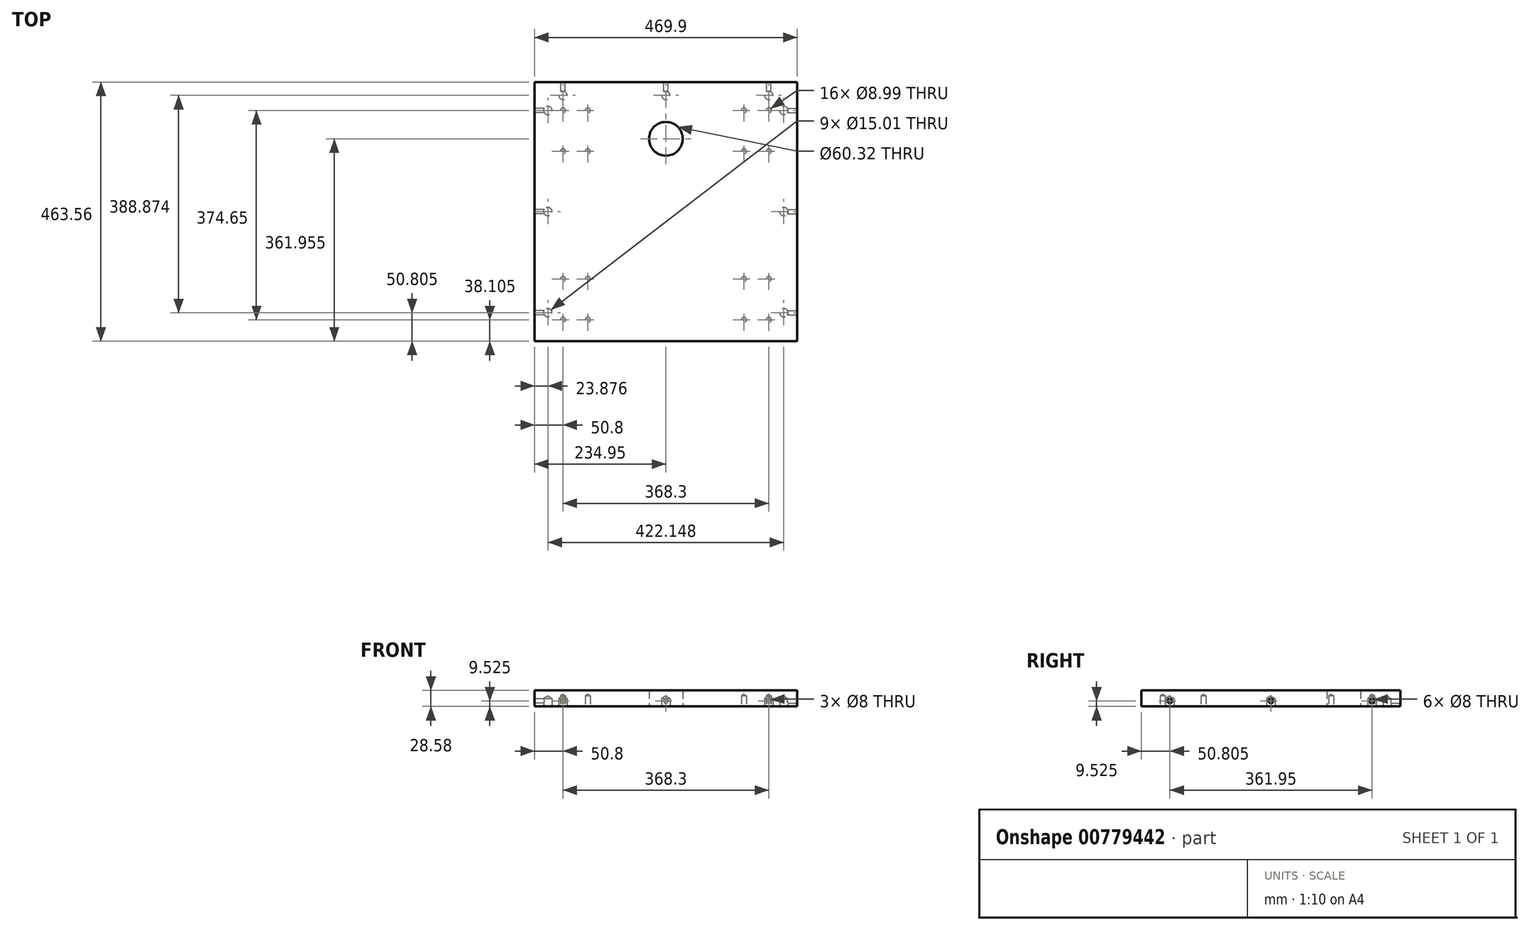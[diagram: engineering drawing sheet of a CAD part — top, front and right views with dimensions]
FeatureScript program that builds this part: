
annotation { "Feature Type Name" : "Feature", "Feature Type Description" : "" }
export const myFeature = defineFeature(function(context is Context, id is Id, definition is map)
    precondition{}
    {
        {
            var Q0;
            Q0=qCreatedBy(makeId("Top.planeOp"),FACE);
            var sketch = newSketch(context, id + "F0", { "sketchPlane" : qUnion([Q0])});
            skLineSegment(sketch, "E0.bottom", {"start": v(234.95, 231.78) * mm, "end": v(-234.95, 231.78) * mm});
            skLineSegment(sketch, "E0.top", {"start": v(234.95, -231.78) * mm, "end": v(-234.95, -231.78) * mm});
            skLineSegment(sketch, "E0.left", {"start": v(234.95, 231.77) * mm, "end": v(234.95, -231.78) * mm});
            skLineSegment(sketch, "E0.right", {"start": v(-234.95, 231.78) * mm, "end": v(-234.95, -231.78) * mm});
            skPoint(sketch, "E0.middle", {"position": v(0, 0) * mm});
            skSolve(sketch);
        }
        {
            var Q0;
            Q0=makeQuery(id+"F0.imprint","IMPRINT",FACE,{"disambiguationData":[TD([[makeQuery(id+"F0.imprint","IMPRINT",EDGE,{"derivedFrom":sQuery(id+"F0.wireOp",EDGE,"E0.bottom")}),1.0]])]});
            extrude(context, id + "F1", {"entities" : qUnion([Q0]), "depth" : 19.05 * mm, "offsetDistance" : 25.4 * mm});
        }
        {
            var Q0;
            Q0=makeQuery(id+"F1.opExtrude","CAP_FACE",FACE,{"disambiguationData":[OSD([sQuery(id+"F0.wireOp",EDGE,"E0.bottom"),sQuery(id+"F0.wireOp",EDGE,"E0.top"),sQuery(id+"F0.wireOp",EDGE,"E0.left"),sQuery(id+"F0.wireOp",EDGE,"E0.right")])],"isStart":true});
            var sketch = newSketch(context, id + "F2", { "sketchPlane" : qUnion([Q0])});
            skLineSegment(sketch, "E1", {"start": v(-234.95, 231.78) * mm, "end": v(-211.07, 231.78) * mm});
            skLineSegment(sketch, "E2", {"start": v(-211.07, 231.78) * mm, "end": v(-211.07, 180.97) * mm});
            skLineSegment(sketch, "E3", {"start": v(-234.95, -231.78) * mm, "end": v(-211.07, -231.78) * mm});
            skLineSegment(sketch, "E4", {"start": v(-211.07, -231.78) * mm, "end": v(-211.07, -180.97) * mm});
            skLineSegment(sketch, "E5", {"start": v(234.95, 231.78) * mm, "end": v(234.95, 207.9) * mm});
            skLineSegment(sketch, "E6", {"start": v(234.95, 231.78) * mm, "end": v(211.07, 231.78) * mm});
            skLineSegment(sketch, "E7", {"start": v(211.07, 231.78) * mm, "end": v(211.07, 180.97) * mm});
            skLineSegment(sketch, "E8", {"start": v(234.95, -231.78) * mm, "end": v(211.07, -231.78) * mm});
            skLineSegment(sketch, "E9", {"start": v(211.07, -231.78) * mm, "end": v(211.07, -180.97) * mm});
            skLineSegment(sketch, "E10", {"start": v(-234.95, 0) * mm, "end": v(-211.07, 0) * mm});
            skLineSegment(sketch, "E11", {"start": v(234.95, 0) * mm, "end": v(211.07, 0) * mm});
            skLineSegment(sketch, "E12", {"start": v(0, -231.78) * mm, "end": v(0, -207.9) * mm});
            skLineSegment(sketch, "E13", {"start": v(-234.95, -231.78) * mm, "end": v(-234.95, -207.9) * mm});
            skLineSegment(sketch, "E14", {"start": v(-234.95, -207.9) * mm, "end": v(-184.15, -207.9) * mm});
            skLineSegment(sketch, "E15", {"start": v(234.95, -231.78) * mm, "end": v(234.95, -207.9) * mm});
            skLineSegment(sketch, "E16", {"start": v(234.95, -207.9) * mm, "end": v(184.15, -207.9) * mm});
            skPoint(sketch, "E17", {"position": v(-211.07, 180.97) * mm});
            skPoint(sketch, "E18", {"position": v(211.07, 180.97) * mm});
            skPoint(sketch, "E19", {"position": v(211.07, 0) * mm});
            skPoint(sketch, "E20", {"position": v(-211.07, 0) * mm});
            skPoint(sketch, "E21", {"position": v(-211.07, -180.97) * mm});
            skPoint(sketch, "E22", {"position": v(-184.15, -207.9) * mm});
            skPoint(sketch, "E23", {"position": v(0, -207.9) * mm});
            skPoint(sketch, "E24", {"position": v(184.15, -207.9) * mm});
            skPoint(sketch, "E25", {"position": v(211.07, -180.97) * mm});
            skSolve(sketch);
        }
        {
            var Q0;
            Q0=sQuery(id+"F2.wireOp",VERTEX,"E17");
            var Q1;
            Q1=sQuery(id+"F2.wireOp",VERTEX,"E20");
            var Q2;
            Q2=sQuery(id+"F2.wireOp",VERTEX,"E21");
            var Q3;
            Q3=sQuery(id+"F2.wireOp",VERTEX,"E22");
            var Q4;
            Q4=sQuery(id+"F2.wireOp",VERTEX,"E23");
            var Q5;
            Q5=sQuery(id+"F2.wireOp",VERTEX,"E24");
            var Q6;
            Q6=sQuery(id+"F2.wireOp",VERTEX,"E25");
            var Q7;
            Q7=sQuery(id+"F2.wireOp",VERTEX,"E19");
            var Q8;
            Q8=sQuery(id+"F2.wireOp",VERTEX,"E18");
            var Q9;
            Q9=makeQuery(id+"F1.opExtrude","SWEPT_BODY",BODY,{"disambiguationData":[OSD([sQuery(id+"F0.wireOp",EDGE,"E0.bottom"),sQuery(id+"F0.wireOp",EDGE,"E0.top"),sQuery(id+"F0.wireOp",EDGE,"E0.left"),sQuery(id+"F0.wireOp",EDGE,"E0.right")])]});
            hole(context, id + "F3", {"style" : HoleStyle.SIMPLE, "endStyle" : HoleEndStyle.BLIND, "holeDiameter" : 15 * mm, "majorDiameter" : 6.35 * mm, "holeDepth" : 14.22 * mm, "isTappedThrough" : true, "tappedDepth" : 12.7 * mm, "tapClearance" : 3, "startFromSketch" : true, "locations" : qUnion([Q0, Q1, Q2, Q3, Q4, Q5, Q6, Q7, Q8]), "scope" : qUnion([Q9])});
        }
        {
            var Q0;
            Q0=makeQuery(id+"F1.opExtrude","SWEPT_FACE",FACE,{"disambiguationData":[OSD([sQuery(id+"F0.wireOp",EDGE,"E0.left")])]});
            var sketch = newSketch(context, id + "F4", { "sketchPlane" : qUnion([Q0])});
            skLineSegment(sketch, "E26", {"start": v(-231.77, 9.53) * mm, "end": v(-180.97, 9.53) * mm});
            skLineSegment(sketch, "E27", {"start": v(231.78, 9.53) * mm, "end": v(180.98, 9.53) * mm});
            skLineSegment(sketch, "E28", {"start": v(0, 19.05) * mm, "end": v(0, 9.53) * mm});
            skPoint(sketch, "E29", {"position": v(-180.97, 9.53) * mm});
            skPoint(sketch, "E30", {"position": v(0, 9.53) * mm});
            skPoint(sketch, "E31", {"position": v(180.98, 9.53) * mm});
            skSolve(sketch);
        }
        {
            var Q0;
            Q0=sQuery(id+"F4.wireOp",VERTEX,"E29");
            var Q1;
            Q1=sQuery(id+"F4.wireOp",VERTEX,"E30");
            var Q2;
            Q2=sQuery(id+"F4.wireOp",VERTEX,"E31");
            var Q3;
            Q3=makeQuery(id+"F1.opExtrude","SWEPT_BODY",BODY,{"disambiguationData":[OSD([sQuery(id+"F0.wireOp",EDGE,"E0.bottom"),sQuery(id+"F0.wireOp",EDGE,"E0.top"),sQuery(id+"F0.wireOp",EDGE,"E0.left"),sQuery(id+"F0.wireOp",EDGE,"E0.right")])]});
            hole(context, id + "F5", {"style" : HoleStyle.SIMPLE, "endStyle" : HoleEndStyle.BLIND, "holeDiameter" : 8 * mm, "majorDiameter" : 6.35 * mm, "holeDepth" : 25.4 * mm, "isTappedThrough" : true, "tappedDepth" : 12.7 * mm, "tapClearance" : 3, "startFromSketch" : true, "locations" : qUnion([Q0, Q1, Q2]), "scope" : qUnion([Q3])});
        }
        {
            var Q0;
            Q0=makeQuery(id+"F1.opExtrude","SWEPT_FACE",FACE,{"disambiguationData":[OSD([sQuery(id+"F0.wireOp",EDGE,"E0.bottom")])]});
            var sketch = newSketch(context, id + "F6", { "sketchPlane" : qUnion([Q0])});
            skLineSegment(sketch, "E32", {"start": v(-234.95, 9.53) * mm, "end": v(-184.15, 9.53) * mm});
            skLineSegment(sketch, "E33", {"start": v(234.95, 9.53) * mm, "end": v(184.15, 9.53) * mm});
            skLineSegment(sketch, "E34", {"start": v(0, 19.05) * mm, "end": v(0, 9.53) * mm});
            skPoint(sketch, "E35", {"position": v(-184.15, 9.53) * mm});
            skPoint(sketch, "E36", {"position": v(0, 9.53) * mm});
            skPoint(sketch, "E37", {"position": v(184.15, 9.53) * mm});
            skSolve(sketch);
        }
        {
            var Q0;
            Q0=sQuery(id+"F6.wireOp",VERTEX,"E35");
            var Q1;
            Q1=sQuery(id+"F6.wireOp",VERTEX,"E36");
            var Q2;
            Q2=sQuery(id+"F6.wireOp",VERTEX,"E37");
            var Q3;
            Q3=makeQuery(id+"F1.opExtrude","SWEPT_BODY",BODY,{"disambiguationData":[OSD([sQuery(id+"F0.wireOp",EDGE,"E0.bottom"),sQuery(id+"F0.wireOp",EDGE,"E0.top"),sQuery(id+"F0.wireOp",EDGE,"E0.left"),sQuery(id+"F0.wireOp",EDGE,"E0.right")])]});
            hole(context, id + "F7", {"style" : HoleStyle.SIMPLE, "endStyle" : HoleEndStyle.BLIND, "holeDiameter" : 8 * mm, "majorDiameter" : 6.35 * mm, "holeDepth" : 25.4 * mm, "isTappedThrough" : true, "tappedDepth" : 12.7 * mm, "tapClearance" : 3, "startFromSketch" : true, "locations" : qUnion([Q0, Q1, Q2]), "scope" : qUnion([Q3])});
        }
        {
            var Q0;
            Q0=makeQuery(id+"F1.opExtrude","SWEPT_FACE",FACE,{"disambiguationData":[OSD([sQuery(id+"F0.wireOp",EDGE,"E0.right")])]});
            var sketch = newSketch(context, id + "F8", { "sketchPlane" : qUnion([Q0])});
            skLineSegment(sketch, "E38", {"start": v(-231.77, 9.53) * mm, "end": v(-180.97, 9.53) * mm});
            skLineSegment(sketch, "E39", {"start": v(231.78, 9.53) * mm, "end": v(180.98, 9.53) * mm});
            skLineSegment(sketch, "E40", {"start": v(0, 19.05) * mm, "end": v(0, 9.53) * mm});
            skPoint(sketch, "E41", {"position": v(-180.97, 9.53) * mm});
            skPoint(sketch, "E42", {"position": v(0, 9.53) * mm});
            skPoint(sketch, "E43", {"position": v(180.98, 9.53) * mm});
            skSolve(sketch);
        }
        {
            var Q0;
            Q0=sQuery(id+"F8.wireOp",VERTEX,"E41");
            var Q1;
            Q1=sQuery(id+"F8.wireOp",VERTEX,"E42");
            var Q2;
            Q2=sQuery(id+"F8.wireOp",VERTEX,"E43");
            var Q3;
            Q3=makeQuery(id+"F1.opExtrude","SWEPT_BODY",BODY,{"disambiguationData":[OSD([sQuery(id+"F0.wireOp",EDGE,"E0.bottom"),sQuery(id+"F0.wireOp",EDGE,"E0.top"),sQuery(id+"F0.wireOp",EDGE,"E0.left"),sQuery(id+"F0.wireOp",EDGE,"E0.right")])]});
            hole(context, id + "F9", {"style" : HoleStyle.SIMPLE, "endStyle" : HoleEndStyle.BLIND, "holeDiameter" : 8 * mm, "majorDiameter" : 6.35 * mm, "holeDepth" : 25.4 * mm, "isTappedThrough" : true, "tappedDepth" : 12.7 * mm, "tapClearance" : 3, "startFromSketch" : true, "locations" : qUnion([Q0, Q1, Q2]), "scope" : qUnion([Q3])});
        }
        {
            var Q0;
            Q0=makeQuery(id+"F1.opExtrude","CAP_FACE",FACE,{"disambiguationData":[OSD([sQuery(id+"F0.wireOp",EDGE,"E0.bottom"),sQuery(id+"F0.wireOp",EDGE,"E0.top"),sQuery(id+"F0.wireOp",EDGE,"E0.left"),sQuery(id+"F0.wireOp",EDGE,"E0.right")])],"isStart":false});
            extrude(context, id + "F10", {"entities" : qUnion([Q0]), "operationType" : NewBodyOperationType.ADD, "depth" : 9.52 * mm, "offsetDistance" : 25.4 * mm});
        }
        {
            var Q0;
            Q0=makeQuery(id+"F1.opExtrude","CAP_FACE",FACE,{"disambiguationData":[OSD([sQuery(id+"F0.wireOp",EDGE,"E0.bottom"),sQuery(id+"F0.wireOp",EDGE,"E0.top"),sQuery(id+"F0.wireOp",EDGE,"E0.left"),sQuery(id+"F0.wireOp",EDGE,"E0.right")])],"isStart":true});
            var sketch = newSketch(context, id + "F11", { "sketchPlane" : qUnion([Q0])});
            skLineSegment(sketch, "E44", {"start": v(0, -231.78) * mm, "end": v(0, -130.17) * mm});
            skCircle(sketch, "E45", {"center": v(0, -130.17) * mm, "radius": 30.16 * mm});
            skSolve(sketch);
        }
        {
            var Q0;
            Q0=makeQuery(id+"F11.imprint","IMPRINT",FACE,{"disambiguationData":[TD([[makeQuery(id+"F11.imprint","IMPRINT",EDGE,{"derivedFrom":sQuery(id+"F11.wireOp",EDGE,"E45")}),1.0]])]});
            extrude(context, id + "F12", {"entities" : qUnion([Q0]), "operationType" : NewBodyOperationType.REMOVE, "oppositeDirection" : true, "depth" : 31.75 * mm, "offsetDistance" : 25.4 * mm});
        }
        {
            var Q0;
            Q0=makeQuery(id+"F1.opExtrude","CAP_FACE",FACE,{"disambiguationData":[OSD([sQuery(id+"F0.wireOp",EDGE,"E0.bottom"),sQuery(id+"F0.wireOp",EDGE,"E0.top"),sQuery(id+"F0.wireOp",EDGE,"E0.left"),sQuery(id+"F0.wireOp",EDGE,"E0.right")])],"isStart":true});
            var sketch = newSketch(context, id + "F13", { "sketchPlane" : qUnion([Q0])});
            skLineSegment(sketch, "E46", {"start": v(-234.95, 231.78) * mm, "end": v(-234.95, 193.68) * mm});
            skLineSegment(sketch, "E47", {"start": v(-234.95, 193.68) * mm, "end": v(-184.15, 193.68) * mm});
            skLineSegment(sketch, "E48.bottom", {"start": v(-184.15, 193.68) * mm, "end": v(-139.7, 193.68) * mm});
            skLineSegment(sketch, "E48.top", {"start": v(-184.15, 120.52) * mm, "end": v(-139.7, 120.52) * mm});
            skLineSegment(sketch, "E48.left", {"start": v(-184.15, 193.68) * mm, "end": v(-184.15, 120.52) * mm});
            skLineSegment(sketch, "E48.right", {"start": v(-139.7, 193.68) * mm, "end": v(-139.7, 120.52) * mm});
            skPoint(sketch, "E49", {"position": v(-184.15, 193.68) * mm});
            skPoint(sketch, "E50", {"position": v(-139.7, 193.68) * mm});
            skPoint(sketch, "E51", {"position": v(-139.7, 120.52) * mm});
            skPoint(sketch, "E52", {"position": v(-184.15, 120.52) * mm});
            skLineSegment(sketch, "E53", {"start": v(234.95, 231.78) * mm, "end": v(184.15, 231.78) * mm});
            skLineSegment(sketch, "E54", {"start": v(184.15, 231.78) * mm, "end": v(184.15, 193.68) * mm});
            skLineSegment(sketch, "E55.bottom", {"start": v(184.15, 193.68) * mm, "end": v(139.7, 193.68) * mm});
            skLineSegment(sketch, "E55.top", {"start": v(184.15, 120.52) * mm, "end": v(139.7, 120.52) * mm});
            skLineSegment(sketch, "E55.left", {"start": v(184.15, 193.68) * mm, "end": v(184.15, 120.52) * mm});
            skLineSegment(sketch, "E55.right", {"start": v(139.7, 193.68) * mm, "end": v(139.7, 120.52) * mm});
            skLineSegment(sketch, "E56", {"start": v(-234.95, -231.78) * mm, "end": v(-184.15, -231.78) * mm});
            skLineSegment(sketch, "E57", {"start": v(-184.15, -231.78) * mm, "end": v(-184.15, -180.97) * mm});
            skLineSegment(sketch, "E58.bottom", {"start": v(-184.15, -180.97) * mm, "end": v(-139.7, -180.97) * mm});
            skLineSegment(sketch, "E58.top", {"start": v(-184.15, -107.82) * mm, "end": v(-139.7, -107.82) * mm});
            skLineSegment(sketch, "E58.left", {"start": v(-184.15, -180.97) * mm, "end": v(-184.15, -107.82) * mm});
            skLineSegment(sketch, "E58.right", {"start": v(-139.7, -180.97) * mm, "end": v(-139.7, -107.82) * mm});
            skLineSegment(sketch, "E59", {"start": v(234.95, -231.78) * mm, "end": v(184.15, -231.78) * mm});
            skLineSegment(sketch, "E60", {"start": v(184.15, -231.78) * mm, "end": v(184.15, -180.97) * mm});
            skLineSegment(sketch, "E61.bottom", {"start": v(184.15, -180.97) * mm, "end": v(139.7, -180.97) * mm});
            skLineSegment(sketch, "E61.top", {"start": v(184.15, -107.82) * mm, "end": v(139.7, -107.82) * mm});
            skLineSegment(sketch, "E61.left", {"start": v(184.15, -180.97) * mm, "end": v(184.15, -107.82) * mm});
            skLineSegment(sketch, "E61.right", {"start": v(139.7, -180.97) * mm, "end": v(139.7, -107.82) * mm});
            skPoint(sketch, "E62", {"position": v(-184.15, -107.82) * mm});
            skPoint(sketch, "E63", {"position": v(-139.7, -107.82) * mm});
            skPoint(sketch, "E64", {"position": v(-139.7, -180.97) * mm});
            skPoint(sketch, "E65", {"position": v(-184.15, -180.97) * mm});
            skPoint(sketch, "E66", {"position": v(139.7, -180.97) * mm});
            skPoint(sketch, "E67", {"position": v(184.15, -180.97) * mm});
            skPoint(sketch, "E68", {"position": v(184.15, -107.82) * mm});
            skPoint(sketch, "E69", {"position": v(139.7, -107.82) * mm});
            skPoint(sketch, "E70", {"position": v(139.7, 120.52) * mm});
            skPoint(sketch, "E71", {"position": v(139.7, 193.68) * mm});
            skPoint(sketch, "E72", {"position": v(184.15, 193.68) * mm});
            skPoint(sketch, "E73", {"position": v(184.15, 120.52) * mm});
            skSolve(sketch);
        }
        {
            var Q0;
            Q0=sQuery(id+"F13.wireOp",VERTEX,"E47.end");
            var Q1;
            Q1=sQuery(id+"F13.wireOp",VERTEX,"E48.bottom.end");
            var Q2;
            Q2=sQuery(id+"F13.wireOp",VERTEX,"E51");
            var Q3;
            Q3=sQuery(id+"F13.wireOp",VERTEX,"E48.top.start");
            var Q4;
            Q4=sQuery(id+"F13.wireOp",VERTEX,"E71");
            var Q5;
            Q5=sQuery(id+"F13.wireOp",VERTEX,"E72");
            var Q6;
            Q6=sQuery(id+"F13.wireOp",VERTEX,"E73");
            var Q7;
            Q7=sQuery(id+"F13.wireOp",VERTEX,"E55.top.end");
            var Q8;
            Q8=sQuery(id+"F13.wireOp",VERTEX,"E68");
            var Q9;
            Q9=sQuery(id+"F13.wireOp",VERTEX,"E69");
            var Q10;
            Q10=sQuery(id+"F13.wireOp",VERTEX,"E66");
            var Q11;
            Q11=sQuery(id+"F13.wireOp",VERTEX,"E60.end");
            var Q12;
            Q12=sQuery(id+"F13.wireOp",VERTEX,"E63");
            var Q13;
            Q13=sQuery(id+"F13.wireOp",VERTEX,"E62");
            var Q14;
            Q14=sQuery(id+"F13.wireOp",VERTEX,"E57.end");
            var Q15;
            Q15=sQuery(id+"F13.wireOp",VERTEX,"E64");
            var Q16;
            Q16=makeQuery(id+"F1.opExtrude","SWEPT_BODY",BODY,{"disambiguationData":[OSD([sQuery(id+"F0.wireOp",EDGE,"E0.bottom"),sQuery(id+"F0.wireOp",EDGE,"E0.top"),sQuery(id+"F0.wireOp",EDGE,"E0.left"),sQuery(id+"F0.wireOp",EDGE,"E0.right")])]});
            hole(context, id + "F14", {"style" : HoleStyle.SIMPLE, "endStyle" : HoleEndStyle.BLIND, "holeDiameter" : 9 * mm, "majorDiameter" : 6.35 * mm, "holeDepth" : 19.05 * mm, "isTappedThrough" : true, "tappedDepth" : 12.7 * mm, "tapClearance" : 3, "startFromSketch" : true, "locations" : qUnion([Q0, Q1, Q2, Q3, Q4, Q5, Q6, Q7, Q8, Q9, Q10, Q11, Q12, Q13, Q14, Q15]), "scope" : qUnion([Q16])});
        }
    });
